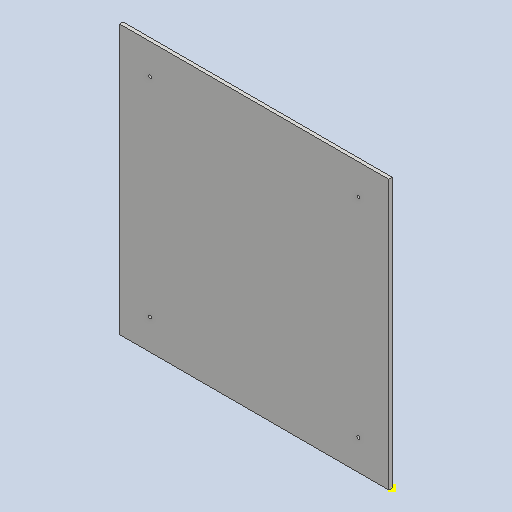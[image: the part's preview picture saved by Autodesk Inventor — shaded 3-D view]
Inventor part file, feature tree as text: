
AUTODESK INVENTOR PART (.ipt)
format: ipt  version: 2023 (Build 270158000, 158)  size: 97,792 bytes
history: native  units: mm
features: sketch x2, extrude x1
ambient origin geometry x8: Origin, YZ Plane, XZ Plane, XY Plane, X Axis, Y Axis, Z Axis, Center Point
bodies: Solid1 (feature_tree)
feature tree (3):
  extrude  "Extrusion1"  Depth=310.0mm
  sketch  "Sketch2"  dims[d2=240.0mm d3=240.0mm d4=240.0mm d5=240.0mm d6=35.0mm d7=35.0mm d8=3.5mm d9=3.5mm d10=3.5mm d11=3.5mm d12=4.0mm d13=0.0mm]
  sketch  "Sketch1"  dims[d0=310.0mm d1=310.0mm]
